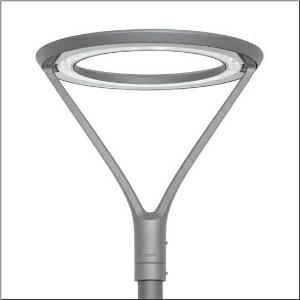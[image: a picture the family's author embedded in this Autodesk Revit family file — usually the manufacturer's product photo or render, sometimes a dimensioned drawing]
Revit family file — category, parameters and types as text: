
# Revit family: dl_r__20_led___st1_2a_5xa512832a008p_5fe4
name_source: partatom
category: Lighting Fixtures
units: mm (PartAtom-declared; Revit-internal decimal feet)

## family parameters
Cut with Voids When Loaded = No
Host = Face
Light Source = No
Part Type = Normal
Room Calculation Point = No
Round Connector Dimension = Use Diameter
Shared = No

## types (1)
- --- (1 x LED, 4290 lm, 51.4 W, 2200K)
    Apparent Load = 51 VA
    CIE Flux Codes = 31 69 96 100 100
    Color Rendering = 70
    Color Temperature = 2200K
    Default Elevation = 1800 mm
    Description = DL® 20 LED, mast luminaire, primary light control with reflector, highly specular, primary optical cover: cover, of toughened safety glass of clear glass with excellent transmission level, light distribution: ST1.2a, light emission: direct distribution, primary light characteristic: asymmetric, installation type: post-top, LED, High Power LED, rated luminous flux: 4.180lm, luminous efficacy: 79lm/W, light colour: 722, colour temperature: 2200K, control gear: ECG Plus, control: flexible luminous flux parameterisation, time-dependent luminous flux control, constant luminous flux control, digital communication interface, power reduction, overheat protection, electronic power reduction, mains connection: 220..240V, 50/60Hz, connection cable pre-assembled, cable length: 5m, start of lifetime: 53W, end of lifetime: 54W, reduction: 24W, luminaire housing, upper part, of cast aluminium, powder-coated, Siteco® metallic grey (DB 702S), diameter: 690mm, height: 690mm, spigot size: 76mm (post-top), luminaire housing, of cast aluminium, powder-coated, Siteco® metallic grey (DB 702S), protection rating (complete): IP66, insulation class (complete): insulation class II (safety insulation), certification: CE, ENEC, VDE, impact resistance: IK08, permissible operating ambient temperature: -25..+30°C, standard-compliant lighting for roads and squares, packaging unit: 1 piece

Light Distribution: ST1.2a
    Height = 690 mm
    Lamp = 1 x LED
    Lamp Light Flux = 4290 lm
    Lamp Power = 51.4 W
    Lamp count = 1
    Length = 690 mm
    Luminous efficacy = 83 lm/W
    Manufacturer = Siteco
    ModVariant = No
    Model = 5XA512832A008P
    Number of Poles = 1
    OnlyDefault = Yes
    Power Factor = 1
    Product Name = DL® 20 LED | ST1.2a
    Product group = mast luminaire | pylon top
    ProductGroupID = 6100
    Protection Class = Protection class II
    Protection Degree = IP 66
    RLX_Detail_Level = 1
    RlxData = <blob elided: 206573 chars, md5=3920868e>
    Socket = socket
    Standby Power = 0 W
    System Light Flux = 4290 lm
    System Power = 51 W
    Type Comments = factory setting: luminous flux: 100 % | dim-lin: 254 | 683 mA
    Type Image = l_1006001.jpg
    URL = http://relux.com
    VarID = @adj_118309
    Voltage = 0 V
    Weight = 0.00 kg
    Width = 0 mm  [stored 0 ft]

note: [stored X ft] marks values corroborated as IEEE doubles in the binary element streams (Revit-internal decimal feet)

## geometry (parser evidence)
native form markers: Blend x4, Sweep x11
no freeform markers — native parametric forms only
